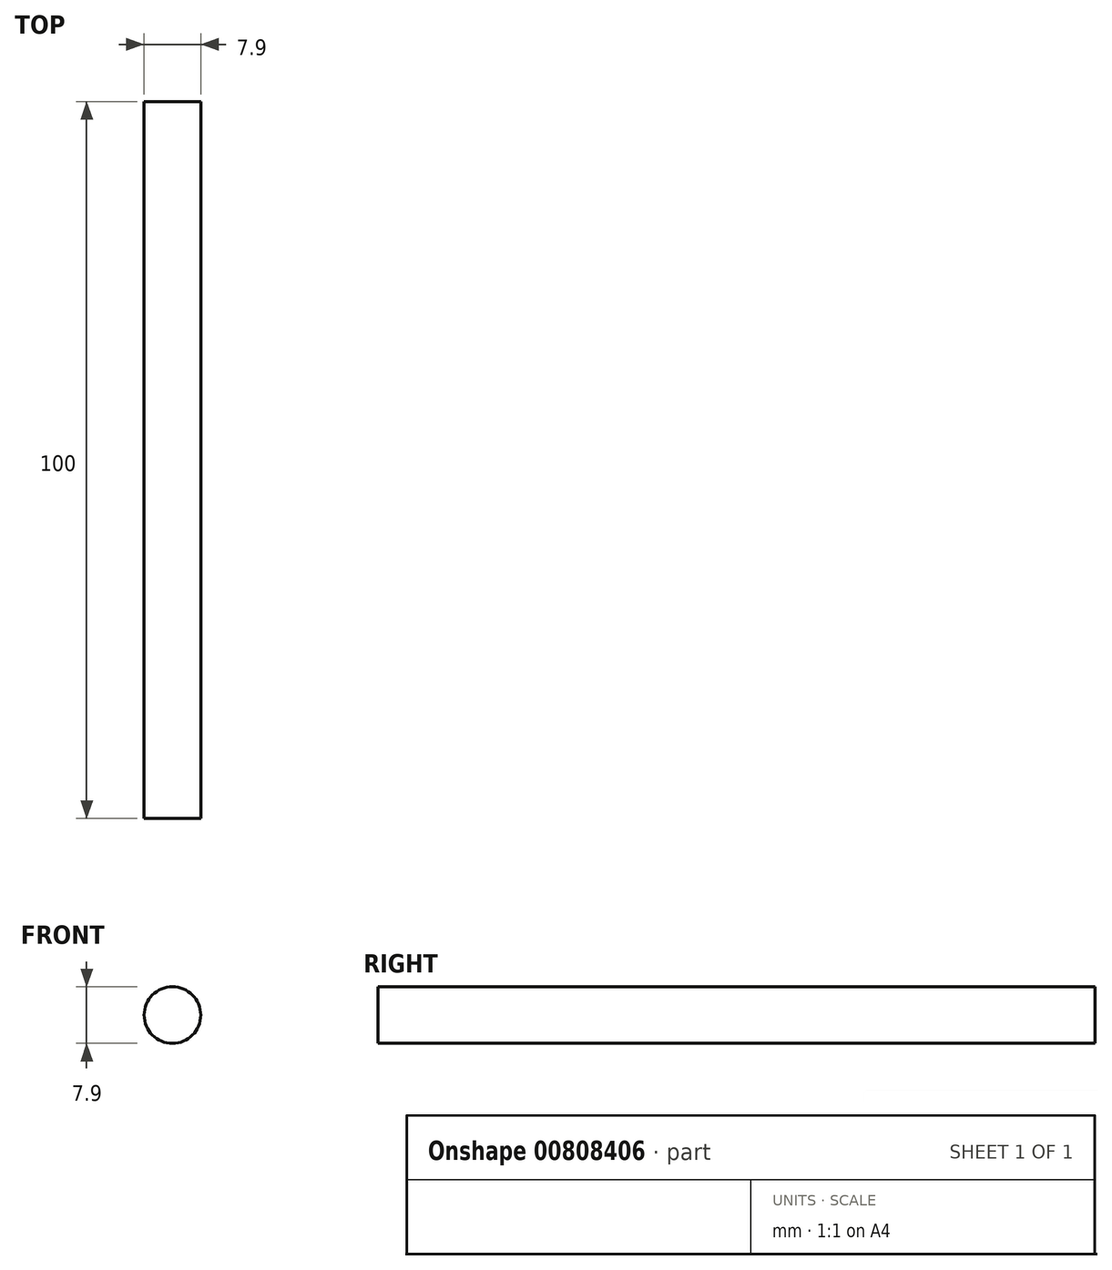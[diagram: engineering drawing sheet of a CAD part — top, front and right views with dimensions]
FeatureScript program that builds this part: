
annotation { "Feature Type Name" : "Feature", "Feature Type Description" : "" }
export const myFeature = defineFeature(function(context is Context, id is Id, definition is map)
    precondition{}
    {
        {
            var Q0;
            Q0=qCreatedBy(makeId("Front.planeOp"),FACE);
            var sketch = newSketch(context, id + "F0", { "sketchPlane" : qUnion([Q0])});
            skCircle(sketch, "E0", {"center": v(0, 0) * mm, "radius": 3.95 * mm});
            skSolve(sketch);
        }
        {
            var Q0;
            Q0=makeQuery(id+"F0.imprint","IMPRINT",FACE,{"disambiguationData":[TD([[makeQuery(id+"F0.imprint","IMPRINT",EDGE,{"derivedFrom":sQuery(id+"F0.wireOp",EDGE,"E0")}),1.0]])]});
            extrude(context, id + "F1", {"entities" : qUnion([Q0]), "depth" : 100 * mm, "offsetDistance" : 25 * mm});
        }
    });
